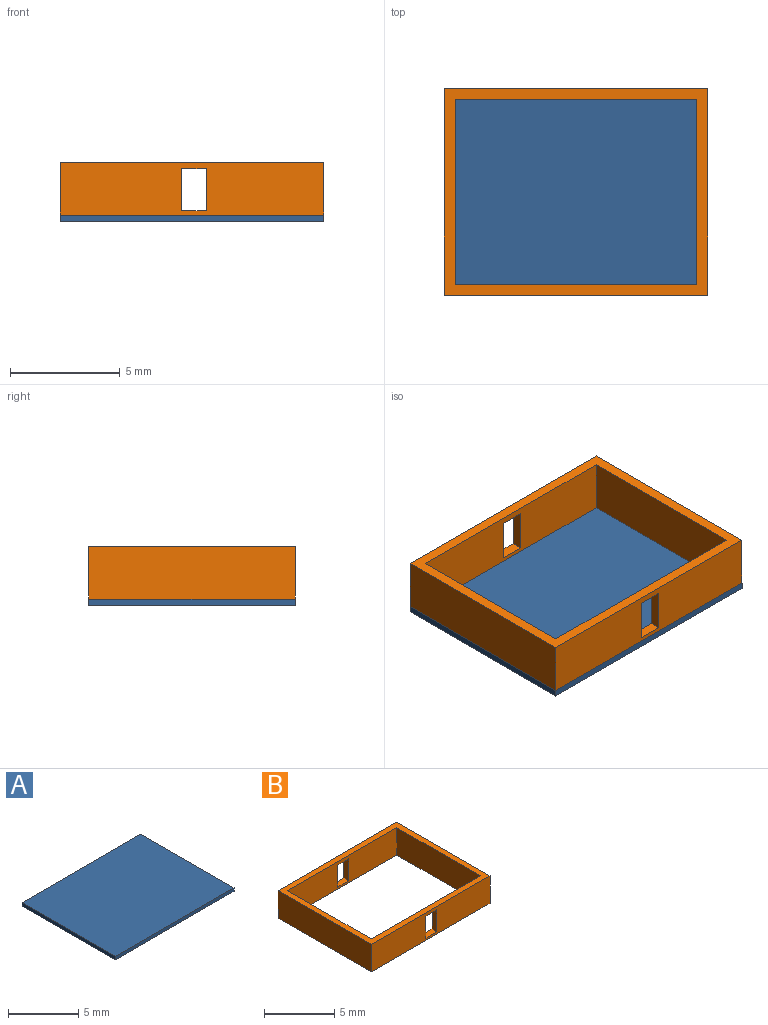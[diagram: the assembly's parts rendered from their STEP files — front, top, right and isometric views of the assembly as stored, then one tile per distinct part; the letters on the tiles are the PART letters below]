
ASSEMBLY  parts=2 mates=1
PART A: 6 faces, bbox 12x9.4x0.3 mm
  f0: plane 9.4x0.3mm, normal (-1,0,0), area 2.8mm2, adj f1,f3,f4,f5
  f1: plane 12x0.3mm, normal (0,-1,0), area 3.6mm2, adj f0,f2,f4,f5
  f2: plane 9.4x0.3mm, normal (1,0,0), area 2.8mm2, adj f1,f3,f4,f5
  f3: plane 12x0.3mm, normal (0,1,0), area 3.6mm2, adj f0,f2,f4,f5
  f4: plane 12x9.4mm, normal (0,0,-1), area 112.8mm2, adj f0,f1,f2,f3
  f5: plane 12x9.4mm, normal (0,0,1), area 112.8mm2, adj f0,f1,f2,f3
PART B: 18 faces, bbox 12x9.4x2.4 mm
  f0: plane 11.02x2.4mm, normal (0,1,0), area 24.3mm2, adj f4,f5,f8,f9,f14,f15,f16,f17
  f1: plane 12x2.4mm, normal (0,-1,0), area 26.7mm2, adj f6,f7,f8,f9,f14,f15,f16,f17
  f2: plane 12x2.4mm, normal (0,1,0), area 26.7mm2, adj f6,f7,f8,f9,f10,f11,f12,f13
  f3: plane 11.02x2.4mm, normal (0,-1,0), area 24.3mm2, adj f4,f5,f8,f9,f10,f11,f12,f13
  f4: plane 8.42x2.4mm, normal (-1,0,0), area 20.2mm2, adj f0,f3,f8,f9
  f5: plane 8.42x2.4mm, normal (1,0,0), area 20.2mm2, adj f0,f3,f8,f9
  f6: plane 9.4x2.4mm, normal (-1,0,0), area 22.6mm2, adj f1,f2,f8,f9
  f7: plane 9.4x2.4mm, normal (1,0,0), area 22.6mm2, adj f1,f2,f8,f9
  f8: plane 12x9.4mm, normal (0,0,1), area 20mm2, adj f0,f1,f2,f3,f4,f5,f6,f7
  f9: plane 12x9.4mm, normal (0,0,-1), area 20mm2, adj f0,f1,f2,f3,f4,f5,f6,f7
  f10: plane 1.92x0.49mm, normal (-1,0,0), area 0.9mm2, adj f2,f3,f11,f13
  f11: plane 1.11x0.49mm, normal (0,0,1), area 0.5mm2, adj f2,f3,f10,f12
  f12: plane 1.92x0.49mm, normal (1,0,0), area 0.9mm2, adj f2,f3,f11,f13
  f13: plane 1.11x0.49mm, normal (0,0,-1), area 0.5mm2, adj f2,f3,f10,f12
  f14: plane 1.11x0.49mm, normal (0,0,-1), area 0.5mm2, adj f0,f1,f15,f17
  f15: plane 1.92x0.49mm, normal (1,0,0), area 0.9mm2, adj f0,f1,f14,f16
  f16: plane 1.11x0.49mm, normal (0,0,1), area 0.5mm2, adj f0,f1,f15,f17
  f17: plane 1.92x0.49mm, normal (-1,0,0), area 0.9mm2, adj f0,f1,f14,f16
PLACE A t=(4.28,-5,5.79)mm
PLACE B t=(4.28,-5,5.79)mm
MATE planar B.f9 <-> A.f5  axis (0,0,-1) through (16.28,-5,5.79)mm
